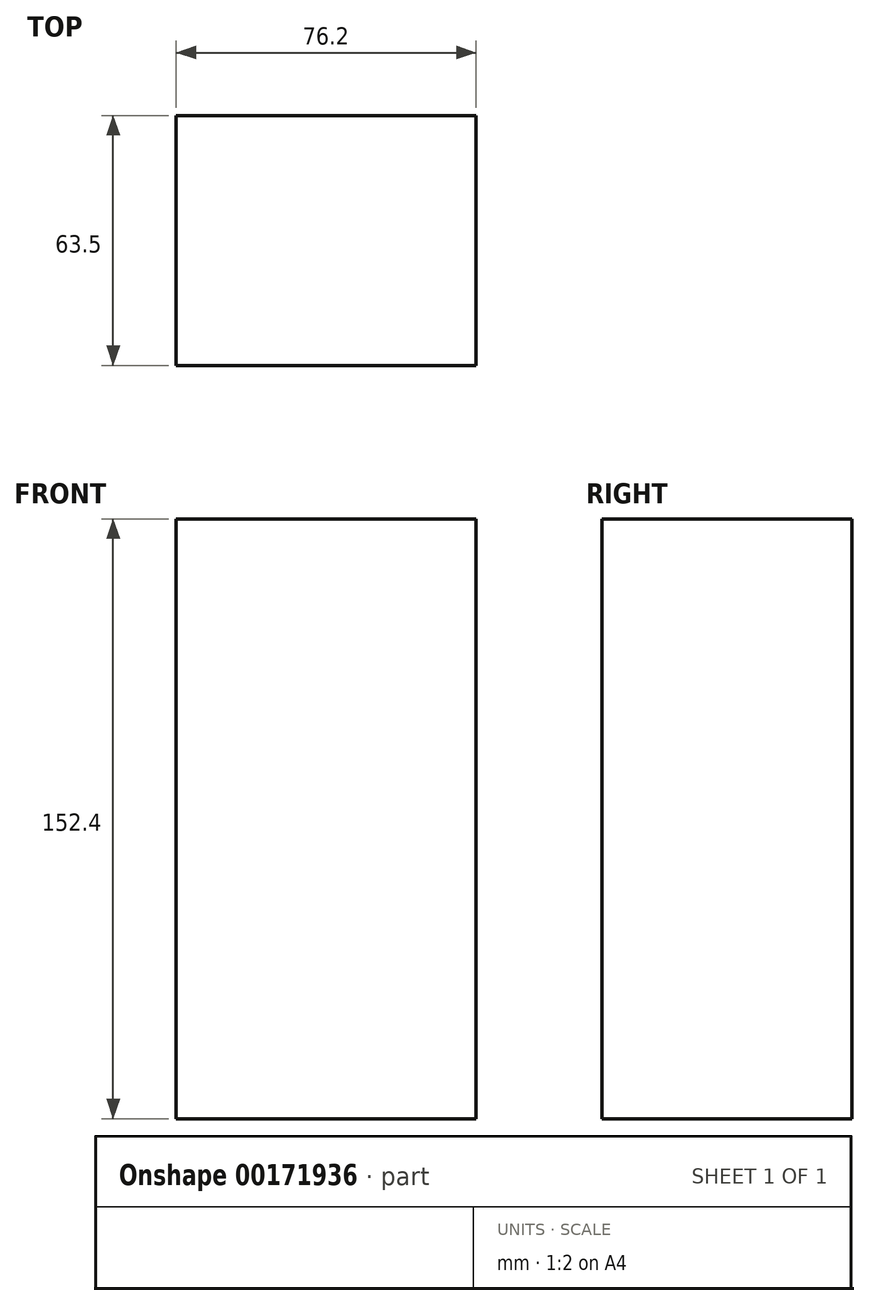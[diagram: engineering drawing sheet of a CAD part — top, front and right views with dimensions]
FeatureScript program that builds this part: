
annotation { "Feature Type Name" : "Feature", "Feature Type Description" : "" }
export const myFeature = defineFeature(function(context is Context, id is Id, definition is map)
    precondition{}
    {
        {
            var Q0;
            Q0=qCreatedBy(makeId("Front.planeOp"),FACE);
            var sketch = newSketch(context, id + "F0", { "sketchPlane" : qUnion([Q0])});
            skLineSegment(sketch, "E0.bottom", {"start": v(152.4, -152.4) * mm, "end": v(-152.4, -152.4) * mm});
            skLineSegment(sketch, "E0.top", {"start": v(152.4, 152.4) * mm, "end": v(-152.4, 152.4) * mm});
            skLineSegment(sketch, "E0.left", {"start": v(152.4, -152.4) * mm, "end": v(152.4, 152.4) * mm});
            skLineSegment(sketch, "E0.right", {"start": v(-152.4, -152.4) * mm, "end": v(-152.4, 152.4) * mm});
            skPoint(sketch, "E0.middle", {"position": v(0, 0) * mm});
            skLineSegment(sketch, "E1.bottom", {"start": v(-132.97, 11.89) * mm, "end": v(-56.77, 11.89) * mm});
            skLineSegment(sketch, "E1.top", {"start": v(-132.97, -140.51) * mm, "end": v(-56.77, -140.51) * mm});
            skLineSegment(sketch, "E1.left", {"start": v(-132.97, 11.89) * mm, "end": v(-132.97, -140.51) * mm});
            skLineSegment(sketch, "E1.right", {"start": v(-56.77, 11.89) * mm, "end": v(-56.77, -140.51) * mm});
            skLineSegment(sketch, "E2.bottom", {"start": v(6.52, 0) * mm, "end": v(57.32, 0) * mm});
            skLineSegment(sketch, "E2.top", {"start": v(6.52, -63.5) * mm, "end": v(57.32, -63.5) * mm});
            skLineSegment(sketch, "E2.left", {"start": v(6.52, 0) * mm, "end": v(6.52, -63.5) * mm});
            skLineSegment(sketch, "E2.right", {"start": v(57.32, 0) * mm, "end": v(57.32, -63.5) * mm});
            skLineSegment(sketch, "E3.bottom", {"start": v(-96.24, 131.9) * mm, "end": v(-63.05, 131.9) * mm});
            skLineSegment(sketch, "E3.top", {"start": v(-96.24, 65.53) * mm, "end": v(-63.05, 65.53) * mm});
            skLineSegment(sketch, "E3.left", {"start": v(-96.24, 131.9) * mm, "end": v(-96.24, 65.53) * mm});
            skLineSegment(sketch, "E3.right", {"start": v(-63.05, 131.9) * mm, "end": v(-63.05, 65.53) * mm});
            skLineSegment(sketch, "E4.bottom", {"start": v(-70.92, 58.21) * mm, "end": v(-87.8, 58.21) * mm});
            skLineSegment(sketch, "E4.top", {"start": v(-70.92, 139.2) * mm, "end": v(-87.8, 139.2) * mm});
            skLineSegment(sketch, "E4.left", {"start": v(-70.92, 58.21) * mm, "end": v(-70.92, 139.2) * mm});
            skLineSegment(sketch, "E4.right", {"start": v(-87.8, 58.21) * mm, "end": v(-87.8, 139.2) * mm});
            skPoint(sketch, "E4.middle", {"position": v(-79.36, 98.71) * mm});
            skPoint(sketch, "E4.middle.positionSnap0", {"position": v(-96.24, 98.71) * mm});
            skPoint(sketch, "E4.centerSnap0", {"position": v(-96.24, 98.71) * mm});
            skLineSegment(sketch, "E5.bottom", {"start": v(-41.13, 129.65) * mm, "end": v(58.44, 129.65) * mm});
            skLineSegment(sketch, "E5.top", {"start": v(-41.13, 107.71) * mm, "end": v(58.44, 107.71) * mm});
            skLineSegment(sketch, "E5.left", {"start": v(-41.13, 129.65) * mm, "end": v(-41.13, 107.71) * mm});
            skLineSegment(sketch, "E5.right", {"start": v(58.44, 129.65) * mm, "end": v(58.44, 107.71) * mm});
            skLineSegment(sketch, "E6.bottom", {"start": v(13.44, 75.09) * mm, "end": v(58.44, 75.09) * mm});
            skLineSegment(sketch, "E6.top", {"start": v(13.44, 40.78) * mm, "end": v(58.44, 40.78) * mm});
            skLineSegment(sketch, "E6.left", {"start": v(13.44, 75.09) * mm, "end": v(13.44, 40.78) * mm});
            skLineSegment(sketch, "E6.right", {"start": v(58.44, 75.09) * mm, "end": v(58.44, 40.78) * mm});
            skCircle(sketch, "E7", {"center": v(34.82, 59.34) * mm, "radius": 6.55 * mm});
            skSolve(sketch);
        }
        {
            var Q0;
            Q0=makeQuery(id+"F0.imprint","IMPRINT",FACE,{"disambiguationData":[TD([[makeQuery(id+"F0.imprint","IMPRINT",EDGE,{"derivedFrom":sQuery(id+"F0.wireOp",EDGE,"E1.bottom")}),-1.0]])]});
            extrude(context, id + "F1", {"entities" : qUnion([Q0]), "endBound" : BoundingType.SYMMETRIC, "depth" : 63.5 * mm});
        }
    });
